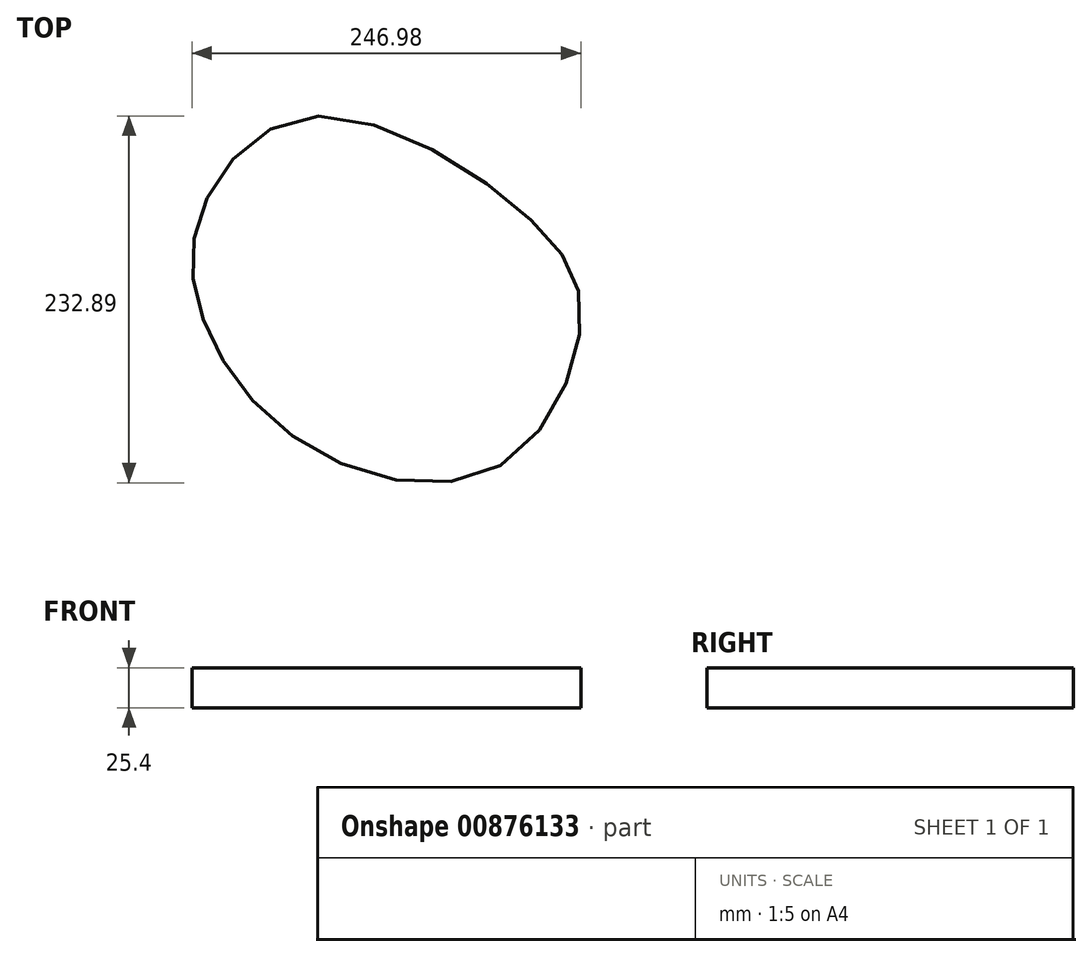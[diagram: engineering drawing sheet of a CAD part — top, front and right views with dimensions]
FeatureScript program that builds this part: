
annotation { "Feature Type Name" : "Feature", "Feature Type Description" : "" }
export const myFeature = defineFeature(function(context is Context, id is Id, definition is map)
    precondition{}
    {
        {
            var Q0;
            Q0=qCreatedBy(makeId("Top.planeOp"),FACE);
            var sketch = newSketch(context, id + "F0", { "sketchPlane" : qUnion([Q0])});
            skFitSpline(sketch, "E0", {"points": [v(-90.45, 0) * mm, v(-90.86, 69.55) * mm, v(-22.88, 128.36) * mm, v(113.42, 67.03) * mm, v(149.5, 0) * mm, v(96.72, -93.96) * mm, v(-23.5, -81) * mm, v(-90.45, 0) * mm]});
            skSolve(sketch);
        }
        {
            var Q0;
            Q0=makeQuery(id+"F0.imprint","IMPRINT",FACE,{"disambiguationData":[TD([[makeQuery(id+"F0.imprint","IMPRINT",EDGE,{"derivedFrom":sQuery(id+"F0.wireOp",EDGE,"E0")}),-1.0]])]});
            extrude(context, id + "F1", {"entities" : qUnion([Q0]), "depth" : 25.4 * mm, "offsetDistance" : 25.4 * mm});
        }
    });
